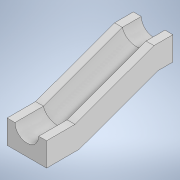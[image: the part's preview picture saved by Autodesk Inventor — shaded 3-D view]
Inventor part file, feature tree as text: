
AUTODESK INVENTOR PART (.ipt)
format: ipt  version: 2021 (Build 250183000, 183)  size: 116,224 bytes
history: native  units: mm
features: sketch x2, sweep x1
ambient origin geometry x8: Origin, YZ Plane, XZ Plane, XY Plane, X Axis, Y Axis, Z Axis, Center Point
bodies: Body1 (feature_tree)
feature tree (3):
  sweep  "Sweep3"
  sketch  "Sketch1"  dims[d0=7.5mm d6=0.0mm]
  sketch  "Sketch2"  dims[d7=0.0mm d8=10.0mm d15=3.490659mm d16=50.0mm d17=20.0mm d20=15.0mm d21=5.0mm d22=5.0mm d23=25.0mm d30=3.75mm d31=11.25mm d32=0.0mm d33=0.0mm]
